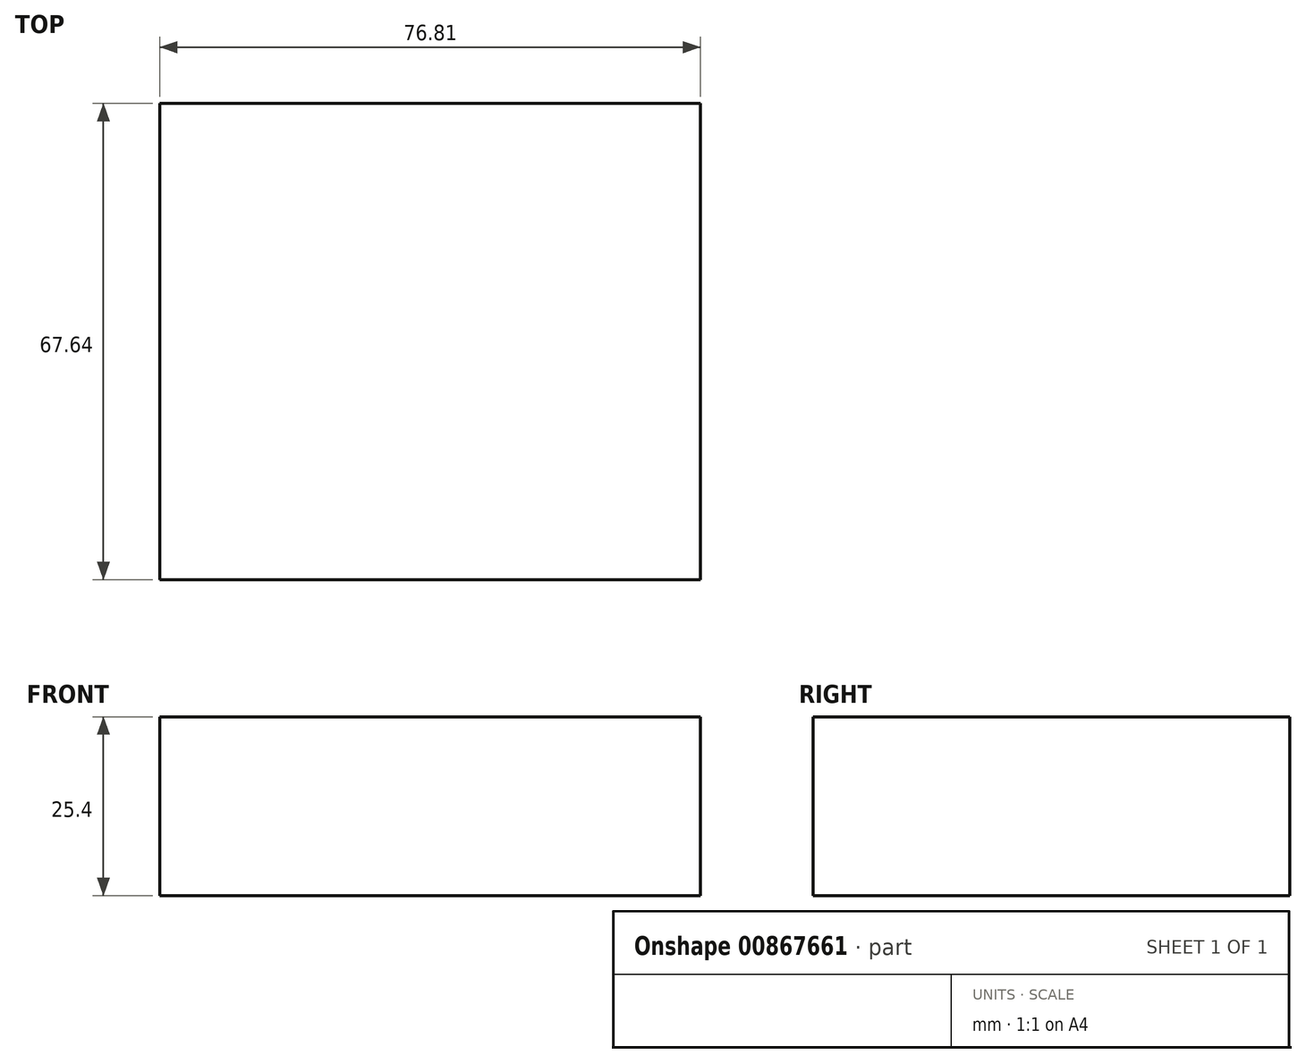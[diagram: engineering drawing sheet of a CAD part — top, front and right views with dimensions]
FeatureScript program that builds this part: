
annotation { "Feature Type Name" : "Feature", "Feature Type Description" : "" }
export const myFeature = defineFeature(function(context is Context, id is Id, definition is map)
    precondition{}
    {
        {
            var Q0;
            Q0=qCreatedBy(makeId("Top.planeOp"),FACE);
            var sketch = newSketch(context, id + "F0", { "sketchPlane" : qUnion([Q0])});
            skLineSegment(sketch, "E0.bottom", {"start": v(-44.91, -35.56) * mm, "end": v(31.9, -35.56) * mm});
            skLineSegment(sketch, "E0.top", {"start": v(-44.91, 32.08) * mm, "end": v(31.9, 32.08) * mm});
            skLineSegment(sketch, "E0.left", {"start": v(-44.91, -35.56) * mm, "end": v(-44.91, 32.08) * mm});
            skLineSegment(sketch, "E0.right", {"start": v(31.9, -35.56) * mm, "end": v(31.9, 32.08) * mm});
            skSolve(sketch);
        }
        {
            var Q0;
            Q0 = qSketchRegion(id + "F0", true);
            var Q1;
            Q1=makeQuery(id+"F0.imprint","IMPRINT",FACE,{"disambiguationData":[TD([[makeQuery(id+"F0.imprint","IMPRINT",EDGE,{"derivedFrom":sQuery(id+"F0.wireOp",EDGE,"E0.bottom")}),1.0]])]});
            extrude(context, id + "F1", {"entities" : qUnion([Q0, Q1]), "depth" : 25.4 * mm, "offsetDistance" : 25.4 * mm});
        }
    });
